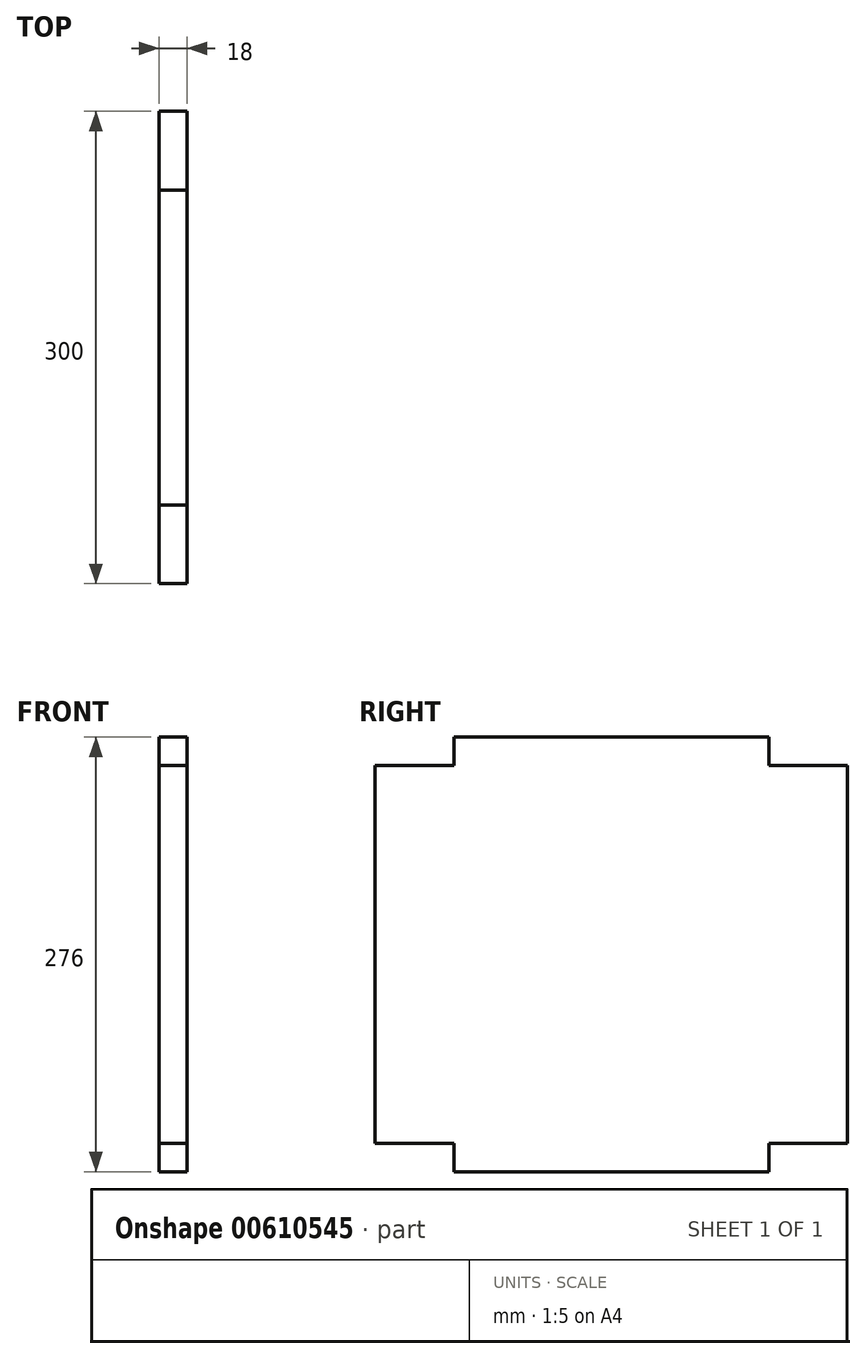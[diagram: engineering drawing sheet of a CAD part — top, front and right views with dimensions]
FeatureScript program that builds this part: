
annotation { "Feature Type Name" : "Feature", "Feature Type Description" : "" }
export const myFeature = defineFeature(function(context is Context, id is Id, definition is map)
    precondition{}
    {
        {
            var Q0;
            Q0=qCreatedBy(makeId("Right.planeOp"),FACE);
            var sketch = newSketch(context, id + "F0", { "sketchPlane" : qUnion([Q0])});
            skLineSegment(sketch, "E0.bottom", {"start": v(-50, -18) * mm, "end": v(-250, -18) * mm});
            skLineSegment(sketch, "E0.top", {"start": v(-50, 258) * mm, "end": v(-250, 258) * mm});
            skLineSegment(sketch, "E0.left", {"start": v(0, 0) * mm, "end": v(0, 240) * mm});
            skLineSegment(sketch, "E0.right", {"start": v(-300, 0) * mm, "end": v(-300, 240) * mm});
            skLineSegment(sketch, "E1.top", {"start": v(0, 240) * mm, "end": v(-50, 240) * mm});
            skLineSegment(sketch, "E1.right", {"start": v(-50, 258) * mm, "end": v(-50, 240) * mm});
            skLineSegment(sketch, "E2.top", {"start": v(-250, 240) * mm, "end": v(-300, 240) * mm});
            skLineSegment(sketch, "E2.left", {"start": v(-250, 258) * mm, "end": v(-250, 240) * mm});
            skLineSegment(sketch, "E3.bottom", {"start": v(-250, 0) * mm, "end": v(-300, 0) * mm});
            skLineSegment(sketch, "E3.left", {"start": v(-250, 0) * mm, "end": v(-250, -18) * mm});
            skLineSegment(sketch, "E4.bottom", {"start": v(0, 0) * mm, "end": v(-50, 0) * mm});
            skLineSegment(sketch, "E4.right", {"start": v(-50, 0) * mm, "end": v(-50, -18) * mm});
            skSolve(sketch);
        }
        {
            var Q0;
            Q0=makeQuery(id+"F0.imprint","IMPRINT",FACE,{"disambiguationData":[TD([[makeQuery(id+"F0.imprint","IMPRINT",EDGE,{"derivedFrom":sQuery(id+"F0.wireOp",EDGE,"E0.bottom")}),-1.0]])]});
            var Q1;
            Q1=sQuery(id+"F0.wireOp",EDGE,"E4.bottom");
            var Q2;
            Q2=sQuery(id+"F0.wireOp",EDGE,"E3.bottom");
            var Q3;
            Q3=sQuery(id+"F0.wireOp",EDGE,"E2.top");
            var Q4;
            Q4=sQuery(id+"F0.wireOp",EDGE,"E1.top");
            var Q5;
            Q5=sQuery(id+"F0.wireOp",EDGE,"E0.right");
            var Q6;
            Q6=sQuery(id+"F0.wireOp",EDGE,"E0.left");
            var Q7;
            Q7=sQuery(id+"F0.wireOp",EDGE,"E0.top");
            var Q8;
            Q8=sQuery(id+"F0.wireOp",EDGE,"E0.bottom");
            var Q9;
            Q9=sQuery(id+"F0.wireOp",EDGE,"E4.right");
            var Q10;
            Q10=sQuery(id+"F0.wireOp",EDGE,"E3.left");
            var Q11;
            Q11=sQuery(id+"F0.wireOp",EDGE,"E2.left");
            var Q12;
            Q12=sQuery(id+"F0.wireOp",EDGE,"E1.right");
            extrude(context, id + "F1", {"entities" : qUnion([Q0]), "surfaceEntities" : qUnion([Q1, Q2, Q3, Q4, Q5, Q6, Q7, Q8, Q9, Q10, Q11, Q12]), "depth" : 18 * mm, "offsetDistance" : 25 * mm});
        }
    });
